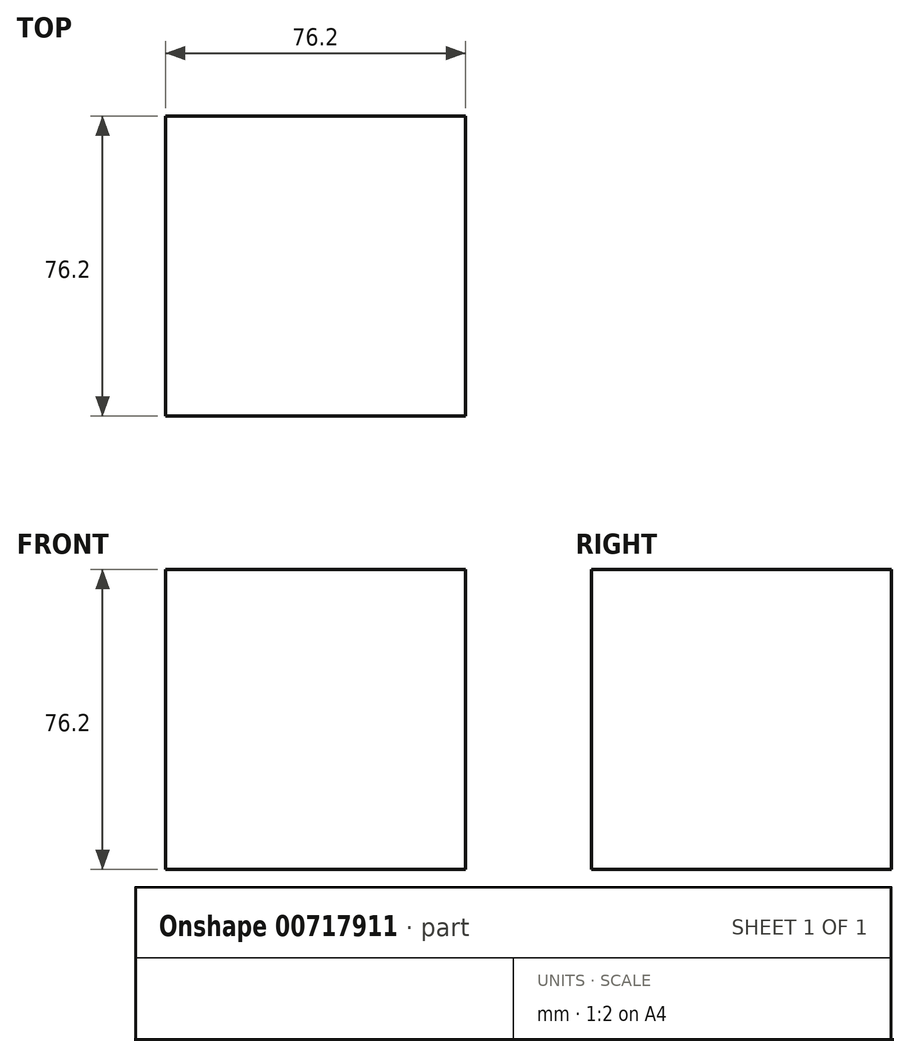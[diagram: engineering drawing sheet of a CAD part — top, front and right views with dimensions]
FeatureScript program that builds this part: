
annotation { "Feature Type Name" : "Feature", "Feature Type Description" : "" }
export const myFeature = defineFeature(function(context is Context, id is Id, definition is map)
    precondition{}
    {
        {
            var Q0;
            Q0=qCreatedBy(makeId("Front.planeOp"),FACE);
            var sketch = newSketch(context, id + "F0", { "sketchPlane" : qUnion([Q0])});
            skLineSegment(sketch, "E0.bottom", {"start": v(-37.17, 51.58) * mm, "end": v(39.03, 51.58) * mm});
            skLineSegment(sketch, "E0.top", {"start": v(-37.17, -24.62) * mm, "end": v(39.03, -24.62) * mm});
            skLineSegment(sketch, "E0.left", {"start": v(-37.17, 51.58) * mm, "end": v(-37.17, -24.62) * mm});
            skLineSegment(sketch, "E0.right", {"start": v(39.03, 51.58) * mm, "end": v(39.03, -24.62) * mm});
            skSolve(sketch);
        }
        {
            var Q0;
            Q0=makeQuery(id+"F0.imprint","IMPRINT",FACE,{"disambiguationData":[TD([[makeQuery(id+"F0.imprint","IMPRINT",EDGE,{"derivedFrom":sQuery(id+"F0.wireOp",EDGE,"E0.bottom")}),-1.0]])]});
            extrude(context, id + "F1", {"entities" : qUnion([Q0]), "depth" : 76.2 * mm, "offsetDistance" : 25.4 * mm});
        }
    });
